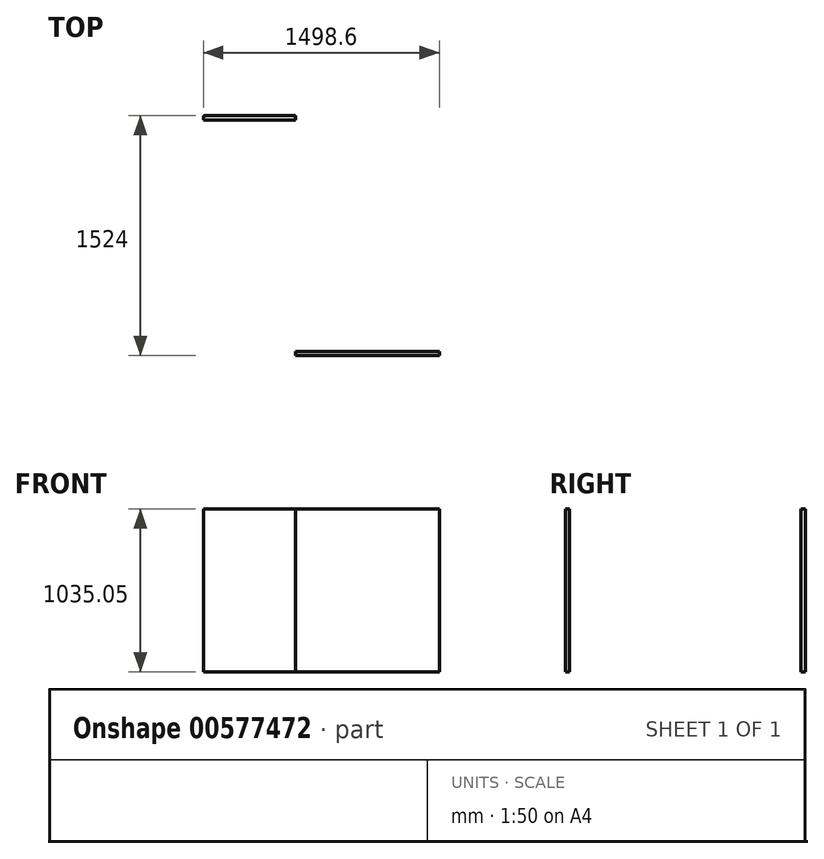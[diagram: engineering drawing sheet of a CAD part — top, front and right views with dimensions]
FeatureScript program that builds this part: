
annotation { "Feature Type Name" : "Feature", "Feature Type Description" : "" }
export const myFeature = defineFeature(function(context is Context, id is Id, definition is map)
    precondition{}
    {
        {
            var Q0;
            Q0=qCreatedBy(makeId("Top.planeOp"),FACE);
            var sketch = newSketch(context, id + "F0", { "sketchPlane" : qUnion([Q0])});
            skLineSegment(sketch, "E0.bottom", {"start": v(304.8, 762) * mm, "end": v(-304.8, 762) * mm});
            skLineSegment(sketch, "E0.top", {"start": v(304.8, -762) * mm, "end": v(-304.8, -762) * mm});
            skLineSegment(sketch, "E0.left", {"start": v(304.8, 762) * mm, "end": v(304.8, -762) * mm});
            skLineSegment(sketch, "E0.right", {"start": v(-304.8, 762) * mm, "end": v(-304.8, -762) * mm});
            skPoint(sketch, "E0.middle", {"position": v(0, 0) * mm});
            skLineSegment(sketch, "E1.bottom", {"start": v(304.8, -762) * mm, "end": v(1219.2, -762) * mm});
            skLineSegment(sketch, "E1.top", {"start": v(304.8, -152.4) * mm, "end": v(1219.2, -152.4) * mm});
            skLineSegment(sketch, "E1.left", {"start": v(304.8, -762) * mm, "end": v(304.8, -152.4) * mm});
            skLineSegment(sketch, "E1.right", {"start": v(1219.2, -762) * mm, "end": v(1219.2, -152.4) * mm});
            skLineSegment(sketch, "E2", {"start": v(304.8, -152.4) * mm, "end": v(609.6, -152.4) * mm});
            skLineSegment(sketch, "E3", {"start": v(609.6, -152.4) * mm, "end": v(609.6, 152.4) * mm});
            skArc(sketch, "E4", {"start": v(609.6, -152.4) * mm, "mid": v(394.07, -63.13) * mm, "end": v(304.8, 152.4) * mm});
            skArc(sketch, "E5", {"start": v(304.8, -762) * mm, "mid": v(-126.25, -583.45) * mm, "end": v(-304.8, -152.4) * mm});
            skLineSegment(sketch, "E6", {"start": v(304.8, -152.4) * mm, "end": v(-304.8, -152.4) * mm});
            skLineSegment(sketch, "E7", {"start": v(304.8, -152.4) * mm, "end": v(-279.4, -152.4) * mm});
            skLineSegment(sketch, "E8", {"start": v(304.8, -152.4) * mm, "end": v(304.8, -736.6) * mm});
            skLineSegment(sketch, "E9", {"start": v(-279.4, -152.4) * mm, "end": v(-279.4, 762) * mm});
            skLineSegment(sketch, "E10", {"start": v(304.8, -736.6) * mm, "end": v(1219.2, -736.6) * mm});
            skArc(sketch, "E11", {"start": v(304.8, -736.6) * mm, "mid": v(-108.3, -565.5) * mm, "end": v(-279.4, -152.4) * mm});
            skLineSegment(sketch, "E12.bottom", {"start": v(1219.2, -152.4) * mm, "end": v(1190.63, -152.4) * mm});
            skLineSegment(sketch, "E12.top", {"start": v(1219.2, -736.6) * mm, "end": v(1190.63, -736.6) * mm});
            skLineSegment(sketch, "E12.left", {"start": v(1219.2, -152.4) * mm, "end": v(1219.2, -736.6) * mm});
            skLineSegment(sketch, "E12.right", {"start": v(1190.63, -152.4) * mm, "end": v(1190.63, -736.6) * mm});
            skLineSegment(sketch, "E13.bottom", {"start": v(-279.4, 762) * mm, "end": v(304.8, 762) * mm});
            skLineSegment(sketch, "E13.top", {"start": v(-279.4, 733.43) * mm, "end": v(304.8, 733.43) * mm});
            skLineSegment(sketch, "E13.left", {"start": v(-279.4, 762) * mm, "end": v(-279.4, 733.43) * mm});
            skLineSegment(sketch, "E13.right", {"start": v(304.8, 762) * mm, "end": v(304.8, 733.42) * mm});
            skSolve(sketch);
        }
        {
            var Q0;
            Q0=makeQuery(id+"F0.imprint","IMPRINT",FACE,{"disambiguationData":[TD([[makeQuery(id+"F0.imprint","IMPRINT",EDGE,{"derivedFrom":sQuery(id+"F0.wireOp",EDGE,"E13.bottom")}),-1.0]])]});
            var Q1;
            {var subQ2=sQuery(id+"F0.wireOp",EDGE,"E0.bottom");Q1=makeQuery(id+"F0.imprint","IMPRINT",FACE,{"disambiguationData":[TD([[makeQuery(id+"F0.imprint","IMPRINT",EDGE,{"derivedFrom":subQ2}),1.0]])]});}
            var Q2;
            Q2=makeQuery(id+"F0.imprint","IMPRINT",FACE,{"disambiguationData":[TD([[makeQuery(id+"F0.imprint","IMPRINT",EDGE,{"derivedFrom":sQuery(id+"F0.wireOp",EDGE,"E1.left")}),1.0]])]});
            var Q3;
            Q3=makeQuery(id+"F0.imprint","IMPRINT",FACE,{"disambiguationData":[TD([[makeQuery(id+"F0.imprint","IMPRINT",EDGE,{"derivedFrom":sQuery(id+"F0.wireOp",EDGE,"E1.bottom")}),1.0]])]});
            var Q4;
            Q4=makeQuery(id+"F0.imprint","IMPRINT",FACE,{"disambiguationData":[TD([[makeQuery(id+"F0.imprint","IMPRINT",EDGE,{"derivedFrom":sQuery(id+"F0.wireOp",EDGE,"E12.bottom")}),1.0]])]});
            extrude(context, id + "F1", {"entities" : qUnion([Q0, Q1, Q2, Q3, Q4]), "depth" : 1035.05 * mm, "offsetDistance" : 25.4 * mm});
        }
    });
